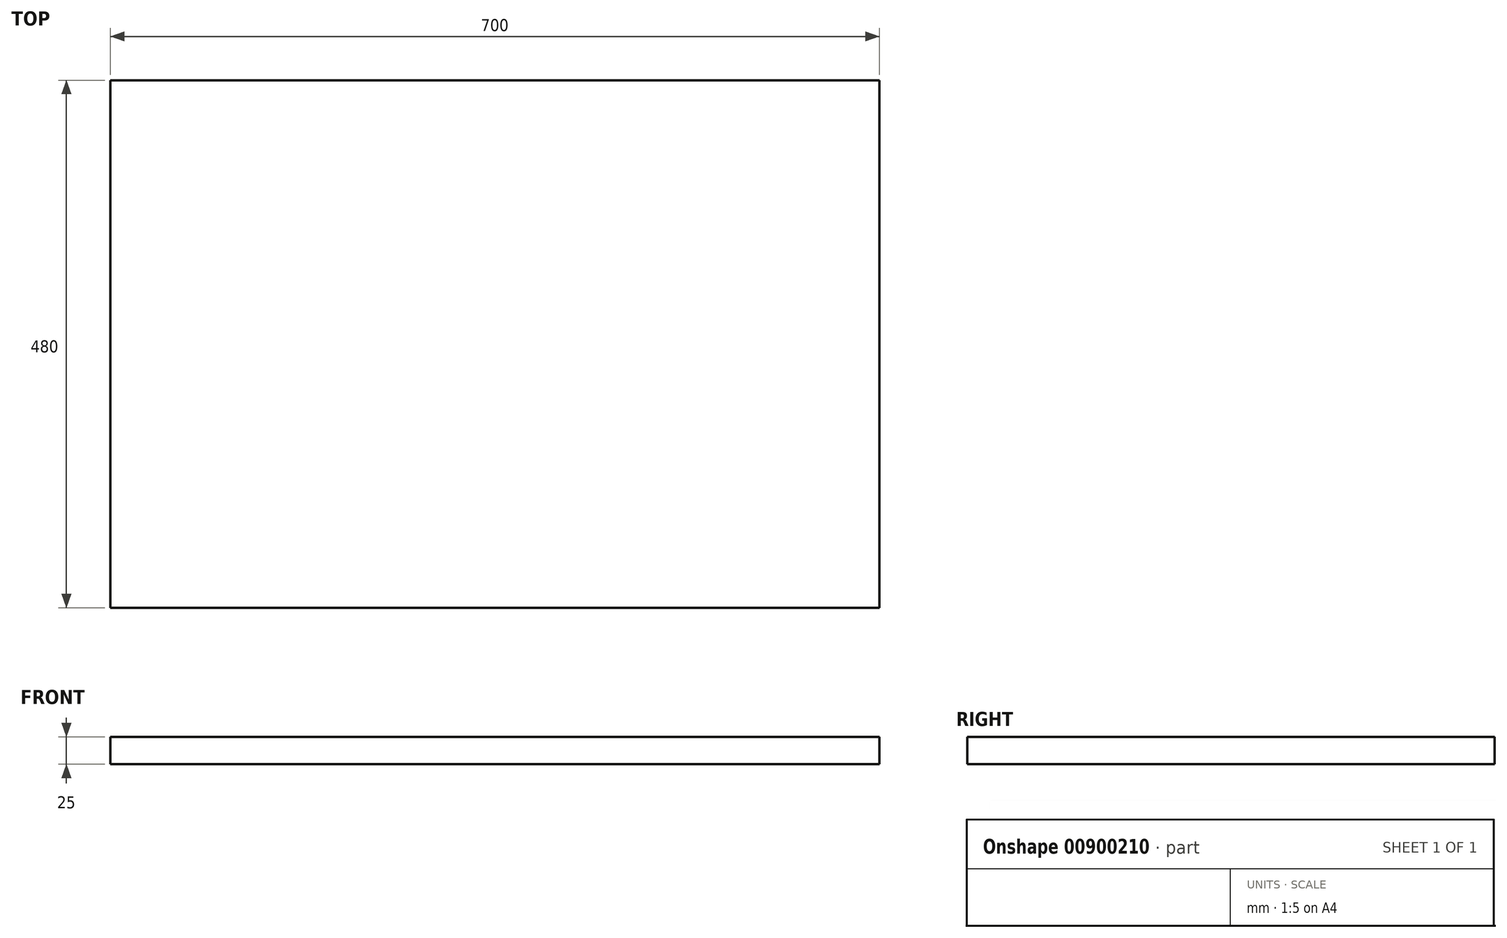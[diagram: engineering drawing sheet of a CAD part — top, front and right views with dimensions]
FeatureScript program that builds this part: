
annotation { "Feature Type Name" : "Feature", "Feature Type Description" : "" }
export const myFeature = defineFeature(function(context is Context, id is Id, definition is map)
    precondition{}
    {
        {
            var Q0;
            Q0=qCreatedBy(makeId("Top.planeOp"),FACE);
            var sketch = newSketch(context, id + "F0", { "sketchPlane" : qUnion([Q0])});
            skLineSegment(sketch, "E0.bottom", {"start": v(-349.88, 258.59) * mm, "end": v(350.12, 258.59) * mm});
            skLineSegment(sketch, "E0.top", {"start": v(-349.88, -221.41) * mm, "end": v(350.12, -221.41) * mm});
            skLineSegment(sketch, "E0.left", {"start": v(-349.88, 258.59) * mm, "end": v(-349.88, -221.41) * mm});
            skLineSegment(sketch, "E0.right", {"start": v(350.12, 258.59) * mm, "end": v(350.12, -221.41) * mm});
            skSolve(sketch);
        }
        {
            var Q0;
            Q0 = qSketchRegion(id + "F0", true);
            extrude(context, id + "F1", {"entities" : qUnion([Q0]), "depth" : 25 * mm, "offsetDistance" : 25 * mm});
        }
    });
